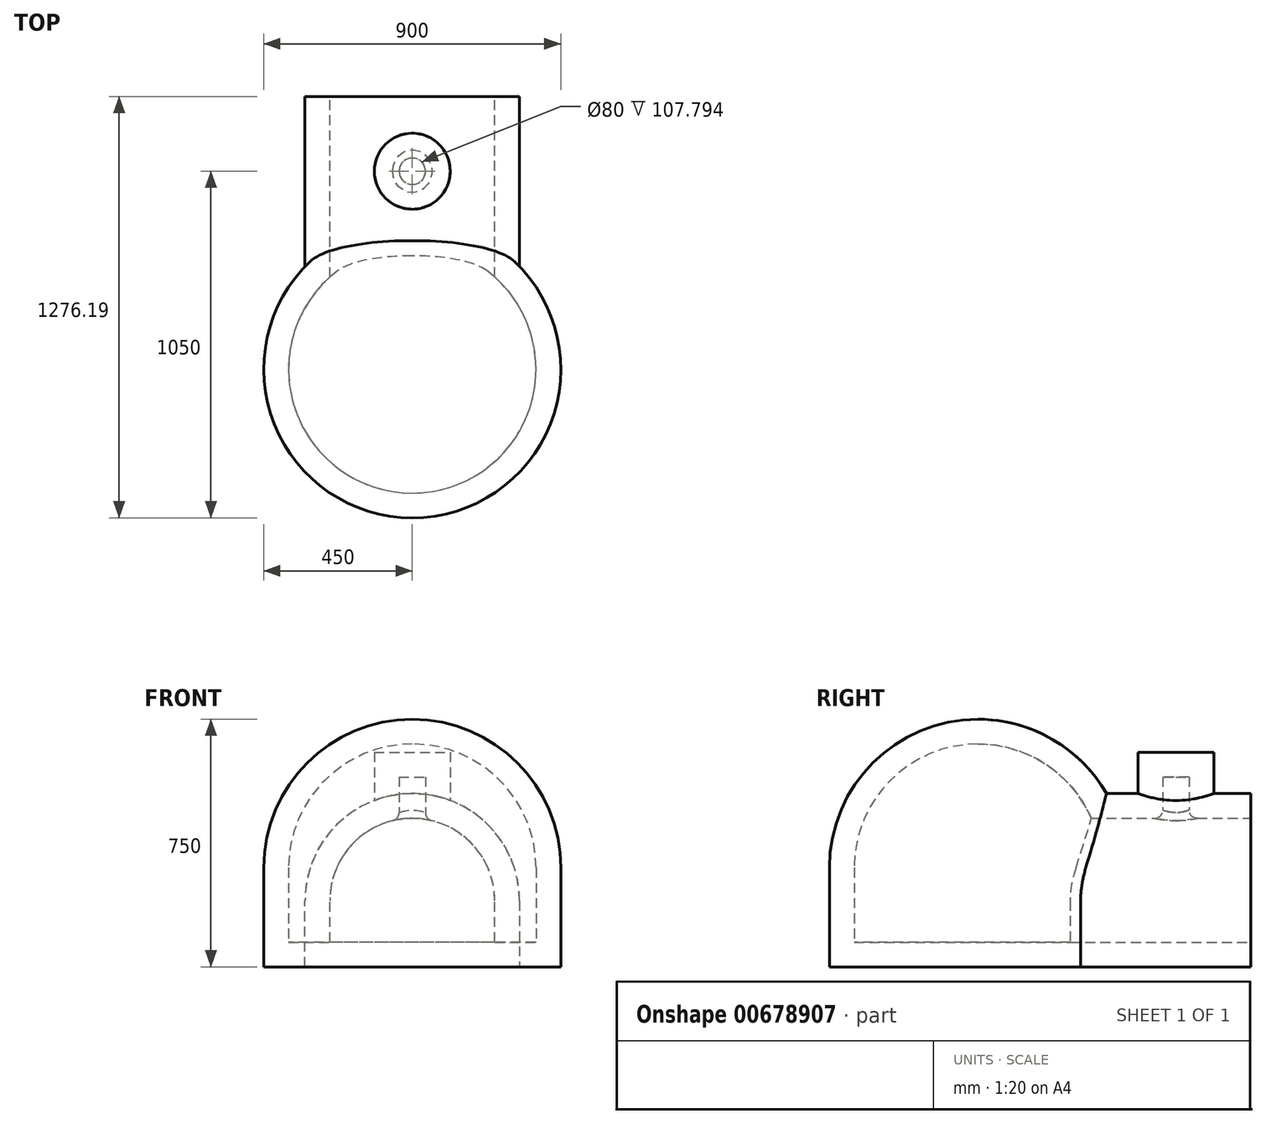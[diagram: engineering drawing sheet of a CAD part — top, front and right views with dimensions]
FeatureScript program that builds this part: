
annotation { "Feature Type Name" : "Feature", "Feature Type Description" : "" }
export const myFeature = defineFeature(function(context is Context, id is Id, definition is map)
    precondition{}
    {
        {
            var Q0;
            Q0=qCreatedBy(makeId("Front.planeOp"),FACE);
            var sketch = newSketch(context, id + "F0", { "sketchPlane" : qUnion([Q0])});
            skLineSegment(sketch, "E0", {"start": v(0, 0) * mm, "end": v(0, 375) * mm, "construction": true});
            skLineSegment(sketch, "E1", {"start": v(0, 0) * mm, "end": v(250, 0) * mm});
            skLineSegment(sketch, "E2", {"start": v(0, 0) * mm, "end": v(-250, 0) * mm});
            skLineSegment(sketch, "E3", {"start": v(250, 0) * mm, "end": v(250, 125) * mm});
            skLineSegment(sketch, "E4", {"start": v(-250, 0) * mm, "end": v(-250, 125) * mm});
            skArc(sketch, "E5", {"start": v(250, 125) * mm, "mid": v(0, 375) * mm, "end": v(-250, 125) * mm});
            skSolve(sketch);
        }
        {
            var Q0;
            Q0=qCreatedBy(makeId("Right.planeOp"),FACE);
            var sketch = newSketch(context, id + "F1", { "sketchPlane" : qUnion([Q0])});
            skPoint(sketch, "E6.orphan", {"position": v(-734.2, 0) * mm});
            skLineSegment(sketch, "E7", {"start": v(0, 0) * mm, "end": v(0, 600) * mm});
            skLineSegment(sketch, "E8", {"start": v(0, 0) * mm, "end": v(375, 0) * mm});
            skLineSegment(sketch, "E9", {"start": v(375, 0) * mm, "end": v(375, 225) * mm});
            skArc(sketch, "E10", {"start": v(375, 225) * mm, "mid": v(265.17, 490.17) * mm, "end": v(0, 600) * mm});
            skSolve(sketch);
        }
        {
            var Q0;
            Q0=qCreatedBy(makeId("Right.planeOp"),FACE);
            var sketch = newSketch(context, id + "F2", { "sketchPlane" : qUnion([Q0])});
            skLineSegment(sketch, "E11", {"start": v(0, 0) * mm, "end": v(826.2, 0) * mm});
            skSolve(sketch);
        }
        {
            var Q0;
            Q0 = qSketchRegion(id + "F0", true);
            var Q1;
            Q1 = qConstructionFilter(qBodyType(qCreatedBy(id + "F0" ,EDGE), BodyType.WIRE), ConstructionObject.NO);
            var Q2;
            Q2 = qConstructionFilter(qBodyType(qCreatedBy(id + "F2" ,EDGE), BodyType.WIRE), ConstructionObject.NO);
            sweep(context, id + "F3", {"profiles" : qUnion([Q0]), "surfaceProfiles" : qUnion([Q1]), "path" : qUnion([Q2])});
        }
        {
            var Q0;
            Q0 = qSketchRegion(id + "F1", true);
            var Q1;
            Q1=sQuery(id+"F1.wireOp",EDGE,"E7");
            revolve(context, id + "F4", {"operationType" : NewBodyOperationType.ADD, "entities" : qUnion([Q0]), "axis" : qUnion([Q1]), "revolveType" : RevolveType.FULL, "surfaceOperationType" : NewSurfaceOperationType.NEW});
        }
        {
            var Q0;
            Q0=makeQuery(id+"F4.boolean.opBoolean","MERGE",FACE,{"derivedFrom":[makeQuery(id+"F3.opSweep","SWEPT_FACE",FACE,{"disambiguationData":[OSD([sQuery(id+"F0.wireOp",EDGE,"E1"),sQuery(id+"F0.wireOp",EDGE,"E2"),sQuery(id+"F2.wireOp",EDGE,"E11")])]}),makeQuery(id+"F4.opRevolve","SWEPT_FACE",FACE,{"disambiguationData":[OSD([sQuery(id+"F1.wireOp",EDGE,"I2wAzcdJ-soIL-oRmt-ZJdK-lZGbjWo5iwh3")])]})]});
            var sketch = newSketch(context, id + "F5", { "sketchPlane" : qUnion([Q0])});
            skCircle(sketch, "E12", {"center": v(0, -600) * mm, "radius": 40 * mm});
            skSolve(sketch);
        }
        {
            var Q0;
            Q0 = qSketchRegion(id + "F5", true);
            extrude(context, id + "F6", {"entities" : qUnion([Q0]), "operationType" : NewBodyOperationType.ADD, "oppositeDirection" : true, "depth" : 500 * mm, "offsetDistance" : 25 * mm});
        }
        {
            var Q0;
            Q0=makeQuery(id+"F4.boolean.opBoolean","INTERSECT",EDGE,{"derivedFrom":[makeQuery(id+"F3.opSweep","SWEPT_FACE",FACE,{"disambiguationData":[OSD([sQuery(id+"F0.wireOp",EDGE,"AK3rwOug-vqaG-WQcE-61q0-UKgrRCKjk3i0"),sQuery(id+"F2.wireOp",EDGE,"E11")])]}),makeQuery(id+"F4.opRevolve","SWEPT_FACE",FACE,{"disambiguationData":[OSD([sQuery(id+"F1.wireOp",EDGE,"BwA6XepY-RFWP-ZZNU-o4qK-JCZfaT67lzG5")])]})]});
            var Q1;
            Q1=makeQuery(id+"F6.boolean.opBoolean","INTERSECT",EDGE,{"derivedFrom":[makeQuery(id+"F3.opSweep","SWEPT_FACE",FACE,{"disambiguationData":[OSD([sQuery(id+"F0.wireOp",EDGE,"AK3rwOug-vqaG-WQcE-61q0-UKgrRCKjk3i0"),sQuery(id+"F2.wireOp",EDGE,"E11")])]}),makeQuery(id+"F6.opExtrude","SWEPT_FACE",FACE,{"disambiguationData":[OSD([sQuery(id+"F5.wireOp",EDGE,"E12")])]})]});
            fillet(context, id + "F7", {"entities" : qUnion([Q0, Q1]), "radius" : 25 * mm, "tangentPropagation" : true, "allowEdgeOverflow" : false});
        }
        {
            var Q0;
            Q0=makeQuery(id+"F3.opSweep","CAP_FACE",FACE,{"disambiguationData":[OSD([sQuery(id+"F0.wireOp",EDGE,"E1"),sQuery(id+"F0.wireOp",EDGE,"AK3rwOug-vqaG-WQcE-61q0-UKgrRCKjk3i0"),sQuery(id+"F0.wireOp",EDGE,"E2"),sQuery(id+"F2.wireOp",VERTEX,"E11.end")])],"isStart":false});
            shell(context, id + "F8", {"entities" : qUnion([Q0]), "thickness" : 75 * mm, "oppositeDirection" : true});
        }
    });
